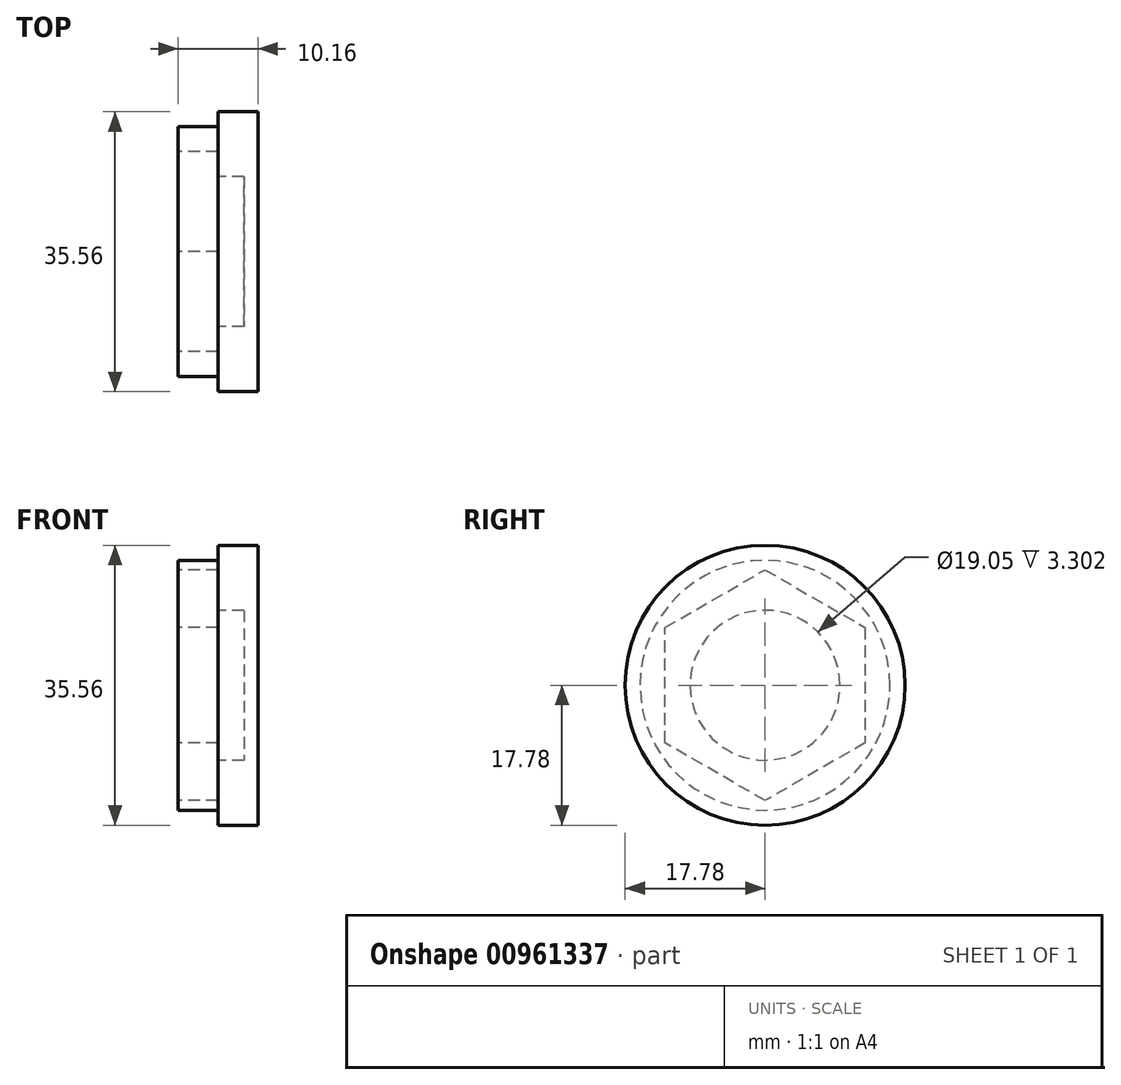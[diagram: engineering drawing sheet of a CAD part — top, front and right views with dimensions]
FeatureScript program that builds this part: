
annotation { "Feature Type Name" : "Feature", "Feature Type Description" : "" }
export const myFeature = defineFeature(function(context is Context, id is Id, definition is map)
    precondition{}
    {
        {
            var Q0;
            Q0=qCreatedBy(makeId("Right.planeOp"),FACE);
            var sketch = newSketch(context, id + "F0", { "sketchPlane" : qUnion([Q0])});
            skCircle(sketch, "E0", {"center": v(0, 0) * mm, "radius": 15.88 * mm});
            skCircle(sketch, "E1.cCircle", {"center": v(0, 0) * mm, "radius": 12.7 * mm, "construction": true});
            skLineSegment(sketch, "E1.0", {"start": v(-12.7, -7.33) * mm, "end": v(-12.7, 7.33) * mm});
            skLineSegment(sketch, "E1.1", {"start": v(-12.7, 7.33) * mm, "end": v(0, 14.66) * mm});
            skLineSegment(sketch, "E1.2", {"start": v(0, 14.66) * mm, "end": v(12.7, 7.33) * mm});
            skLineSegment(sketch, "E1.3", {"start": v(12.7, 7.33) * mm, "end": v(12.7, -7.33) * mm});
            skLineSegment(sketch, "E1.4", {"start": v(12.7, -7.33) * mm, "end": v(0, -14.66) * mm});
            skLineSegment(sketch, "E1.5", {"start": v(0, -14.66) * mm, "end": v(-12.7, -7.33) * mm});
            skPoint(sketch, "E1.0.midPoint", {"position": v(-12.7, 0) * mm});
            skSolve(sketch);
        }
        {
            var Q0;
            Q0=makeQuery(id+"F0.imprint","IMPRINT",FACE,{"disambiguationData":[TD([[makeQuery(id+"F0.imprint","IMPRINT",EDGE,{"derivedFrom":sQuery(id+"F0.wireOp",EDGE,"E0")}),1.0]])]});
            extrude(context, id + "F1", {"entities" : qUnion([Q0]), "depth" : 5.08 * mm, "offsetDistance" : 25.4 * mm});
        }
        {
            var Q0;
            Q0=makeQuery(id+"F1.opExtrude","CAP_FACE",FACE,{"disambiguationData":[OSD([sQuery(id+"F0.wireOp",EDGE,"E0"),sQuery(id+"F0.wireOp",EDGE,"dd3d0266-aebb-4655-b538-b11fd7faddbc.0"),sQuery(id+"F0.wireOp",EDGE,"dd3d0266-aebb-4655-b538-b11fd7faddbc.1"),sQuery(id+"F0.wireOp",EDGE,"dd3d0266-aebb-4655-b538-b11fd7faddbc.2"),sQuery(id+"F0.wireOp",EDGE,"dd3d0266-aebb-4655-b538-b11fd7faddbc.3"),sQuery(id+"F0.wireOp",EDGE,"dd3d0266-aebb-4655-b538-b11fd7faddbc.4"),sQuery(id+"F0.wireOp",EDGE,"dd3d0266-aebb-4655-b538-b11fd7faddbc.5")])],"isStart":false});
            var sketch = newSketch(context, id + "F2", { "sketchPlane" : qUnion([Q0])});
            skCircle(sketch, "E2", {"center": v(0, 0) * mm, "radius": 17.78 * mm});
            skSolve(sketch);
        }
        {
            var Q0;
            Q0 = qSketchRegion(id + "F2", true);
            extrude(context, id + "F3", {"entities" : qUnion([Q0]), "operationType" : NewBodyOperationType.ADD, "depth" : 5.08 * mm, "offsetDistance" : 25.4 * mm});
        }
        {
            var Q0;
            Q0=makeQuery(id+"F3.boolean.opBoolean","SPLIT",FACE,{"disambiguationData":[TD([makeQuery(id+"F1.opExtrude","SWEPT_FACE",FACE,{"disambiguationData":[OSD([sQuery(id+"F0.wireOp",EDGE,"E1.0")])]})])],"derivedFrom":makeQuery(id+"F3.opExtrude","CAP_FACE",FACE,{"disambiguationData":[OSD([sQuery(id+"F2.wireOp",EDGE,"E2")])],"isStart":true})});
            var sketch = newSketch(context, id + "F4", { "sketchPlane" : qUnion([Q0])});
            skCircle(sketch, "E3", {"center": v(0, 0) * mm, "radius": 9.53 * mm});
            skSolve(sketch);
        }
        {
            var Q0;
            Q0=makeQuery(id+"F4.imprint","IMPRINT",FACE,{"disambiguationData":[TD([[makeQuery(id+"F4.imprint","IMPRINT",EDGE,{"derivedFrom":sQuery(id+"F4.wireOp",EDGE,"E3")}),1.0]])]});
            extrude(context, id + "F5", {"entities" : qUnion([Q0]), "operationType" : NewBodyOperationType.REMOVE, "oppositeDirection" : true, "depth" : 3.3 * mm, "offsetDistance" : 25.4 * mm});
        }
    });
